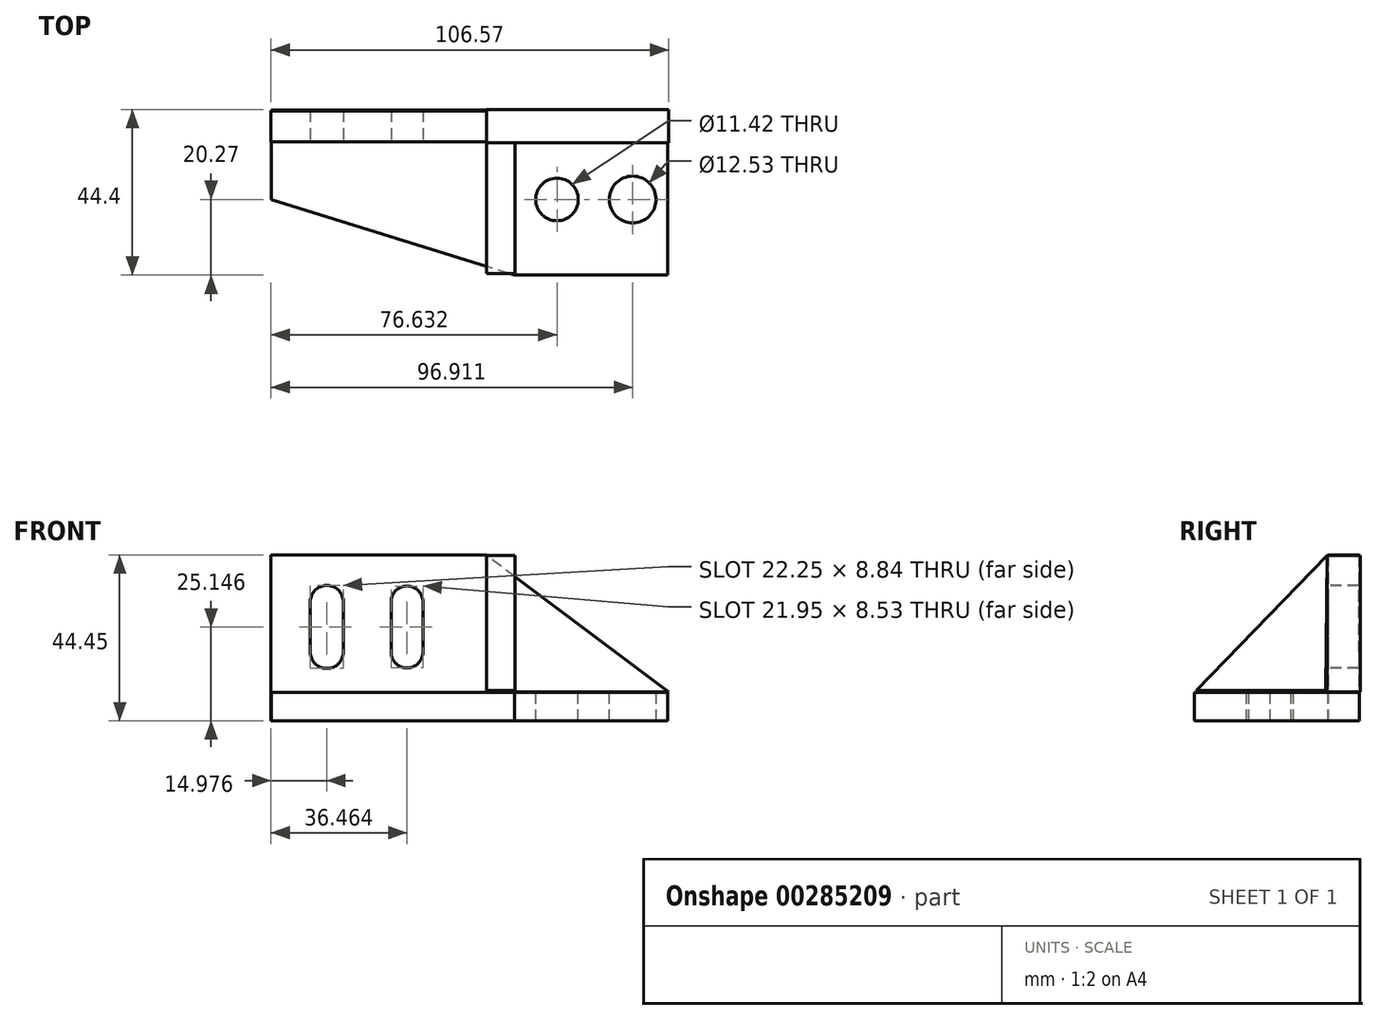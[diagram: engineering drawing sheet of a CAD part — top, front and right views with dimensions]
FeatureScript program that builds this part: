
annotation { "Feature Type Name" : "Feature", "Feature Type Description" : "" }
export const myFeature = defineFeature(function(context is Context, id is Id, definition is map)
    precondition{}
    {
        {
            var Q0;
            Q0=qCreatedBy(makeId("Top.planeOp"),FACE);
            var sketch = newSketch(context, id + "F0", { "sketchPlane" : qUnion([Q0])});
            skLineSegment(sketch, "E0", {"start": v(48.46, -20.27) * mm, "end": v(7.48, -20.27) * mm});
            skLineSegment(sketch, "E1", {"start": v(7.48, -20.27) * mm, "end": v(-57.74, 0) * mm});
            skLineSegment(sketch, "E2", {"start": v(-57.74, 0) * mm, "end": v(-57.74, 23.93) * mm});
            skLineSegment(sketch, "E3", {"start": v(-57.74, 23.93) * mm, "end": v(48.46, 23.93) * mm});
            skLineSegment(sketch, "E4", {"start": v(48.46, 23.93) * mm, "end": v(48.46, -20.27) * mm});
            skSolve(sketch);
        }
        {
            var Q0;
            Q0=makeQuery(id+"F0.imprint","IMPRINT",FACE,{"disambiguationData":[TD([[makeQuery(id+"F0.imprint","IMPRINT",EDGE,{"derivedFrom":sQuery(id+"F0.wireOp",EDGE,"E0")}),-1.0]])]});
            var sketch = newSketch(context, id + "F1", { "sketchPlane" : qUnion([Q0])});
            skLineSegment(sketch, "E5", {"start": v(-57.8, 15.5) * mm, "end": v(0, 15.5) * mm});
            skLineSegment(sketch, "E6", {"start": v(0, 15.5) * mm, "end": v(0, 23.75) * mm});
            skLineSegment(sketch, "E7", {"start": v(-57.8, 15.5) * mm, "end": v(-57.8, 23.75) * mm});
            skLineSegment(sketch, "E8", {"start": v(-57.8, 23.75) * mm, "end": v(0, 23.75) * mm});
            skSolve(sketch);
        }
        {
            var Q0;
            Q0 = qSketchRegion(id + "F1", true);
            extrude(context, id + "F2", {"entities" : qUnion([Q0]), "depth" : 44.45 * mm});
        }
        {
            var Q0;
            Q0=makeQuery(id+"F0.imprint","IMPRINT",FACE,{"disambiguationData":[TD([[makeQuery(id+"F0.imprint","IMPRINT",EDGE,{"derivedFrom":sQuery(id+"F0.wireOp",EDGE,"E0")}),-1.0]])]});
            extrude(context, id + "F3", {"entities" : qUnion([Q0]), "operationType" : NewBodyOperationType.ADD, "depth" : 7.62 * mm});
        }
        {
            var Q0;
            Q0=makeQuery(id+"F3.opExtrude","CAP_FACE",FACE,{"disambiguationData":[OSD([sQuery(id+"F0.wireOp",EDGE,"E0"),sQuery(id+"F0.wireOp",EDGE,"E1"),sQuery(id+"F0.wireOp",EDGE,"E2"),sQuery(id+"F0.wireOp",EDGE,"E3"),sQuery(id+"F0.wireOp",EDGE,"E4")])],"isStart":false});
            var sketch = newSketch(context, id + "F4", { "sketchPlane" : qUnion([Q0])});
            skSolve(sketch);
        }
        {
            var Q0;
            Q0=makeQuery(id+"F2.opExtrude","SWEPT_FACE",FACE,{"disambiguationData":[OSD([sQuery(id+"F1.wireOp",EDGE,"E5")])]});
            var sketch = newSketch(context, id + "F5", { "sketchPlane" : qUnion([Q0])});
            skSolve(sketch);
        }
        {
            var Q0;
            Q0=qCreatedBy(makeId("Front.planeOp"),FACE);
            var sketch = newSketch(context, id + "F6", { "sketchPlane" : qUnion([Q0])});
            skLineSegment(sketch, "E9", {"start": v(0, 44.35) * mm, "end": v(0, 7.77) * mm});
            skLineSegment(sketch, "E10", {"start": v(0, 7.77) * mm, "end": v(48.77, 7.77) * mm});
            skLineSegment(sketch, "E11", {"start": v(48.77, 7.77) * mm, "end": v(0, 44.35) * mm});
            skSolve(sketch);
        }
        {
            var Q0;
            Q0 = qSketchRegion(id + "F6", true);
            extrude(context, id + "F7", {"entities" : qUnion([Q0]), "oppositeDirection" : true, "depth" : 24.13 * mm});
        }
        {
            var Q0;
            Q0=makeQuery(id+"F7.opExtrude","CAP_FACE",FACE,{"disambiguationData":[OSD([sQuery(id+"F6.wireOp",EDGE,"E9"),sQuery(id+"F6.wireOp",EDGE,"E10"),sQuery(id+"F6.wireOp",EDGE,"E11")])],"isStart":true});
            extrude(context, id + "F8", {"entities" : qUnion([Q0]), "operationType" : NewBodyOperationType.REMOVE, "oppositeDirection" : true, "depth" : 15.24 * mm});
        }
        {
            var Q0;
            Q0=qCreatedBy(makeId("Right.planeOp"),FACE);
            var sketch = newSketch(context, id + "F9", { "sketchPlane" : qUnion([Q0])});
            skLineSegment(sketch, "E12", {"start": v(15.24, 44.35) * mm, "end": v(-19.81, 8.08) * mm});
            skLineSegment(sketch, "E13", {"start": v(-19.81, 8.08) * mm, "end": v(14.94, 8.08) * mm});
            skLineSegment(sketch, "E14", {"start": v(14.94, 8.08) * mm, "end": v(15.24, 44.35) * mm});
            skSolve(sketch);
        }
        {
            var Q0;
            Q0=makeQuery(id+"F9.imprint","IMPRINT",FACE,{"disambiguationData":[TD([[makeQuery(id+"F9.imprint","IMPRINT",EDGE,{"derivedFrom":sQuery(id+"F9.wireOp",EDGE,"E12")}),1.0]])]});
            extrude(context, id + "F10", {"entities" : qUnion([Q0]), "operationType" : NewBodyOperationType.ADD, "depth" : 7.62 * mm});
        }
        {
            var Q0;
            {var subQ0=sQuery(id+"F1.wireOp",EDGE,"E5");Q0=makeQuery(id+"F5.imprint","IMPRINT",FACE,{"disambiguationData":[TD([[makeQuery(id+"F5.imprint","IMPRINT",EDGE,{"derivedFrom":makeQuery(id+"F2.opExtrude","CAP_EDGE",EDGE,{"disambiguationData":[OSD([subQ0])],"isStart":false})}),-1.0]])]});}
            var sketch = newSketch(context, id + "F11", { "sketchPlane" : qUnion([Q0])});
            skLineSegment(sketch, "E15", {"start": v(-47.24, 31.85) * mm, "end": v(-47.24, 18.44) * mm});
            skLineSegment(sketch, "E16", {"start": v(-47.24, 18.44) * mm, "end": v(-47.24, 31.85) * mm});
            skLineSegment(sketch, "E17", {"start": v(-38.4, 31.85) * mm, "end": v(-38.4, 18.44) * mm});
            skLineSegment(sketch, "E18", {"start": v(-38.4, 18.44) * mm, "end": v(-38.4, 31.85) * mm});
            skLineSegment(sketch, "E19", {"start": v(-25.6, 31.85) * mm, "end": v(-25.6, 18.44) * mm});
            skLineSegment(sketch, "E20", {"start": v(-25.6, 18.44) * mm, "end": v(-25.6, 31.85) * mm});
            skLineSegment(sketch, "E21", {"start": v(-17.07, 31.85) * mm, "end": v(-17.07, 18.44) * mm});
            skLineSegment(sketch, "E22", {"start": v(-17.07, 18.44) * mm, "end": v(-17.07, 31.85) * mm});
            skArc(sketch, "E23", {"start": v(-47.24, 18.44) * mm, "mid": v(-42.82, 14.02) * mm, "end": v(-38.4, 18.44) * mm});
            skArc(sketch, "E24", {"start": v(-25.6, 18.44) * mm, "mid": v(-21.34, 14.17) * mm, "end": v(-17.07, 18.44) * mm});
            skArc(sketch, "E25", {"start": v(-38.4, 31.85) * mm, "mid": v(-42.82, 36.27) * mm, "end": v(-47.24, 31.85) * mm});
            skArc(sketch, "E26", {"start": v(-17.07, 31.85) * mm, "mid": v(-21.34, 36.12) * mm, "end": v(-25.6, 31.85) * mm});
            skSolve(sketch);
        }
        {
            var Q0;
            Q0 = qSketchRegion(id + "F11", true);
            extrude(context, id + "F12", {"entities" : qUnion([Q0]), "operationType" : NewBodyOperationType.REMOVE, "oppositeDirection" : true, "depth" : 127 * mm});
        }
        {
            var Q0;
            {var subQ3=sQuery(id+"F0.wireOp",EDGE,"E0");Q0=makeQuery(id+"F4.imprint","IMPRINT",FACE,{"disambiguationData":[TD([[makeQuery(id+"F4.imprint","IMPRINT",EDGE,{"derivedFrom":makeQuery(id+"F3.opExtrude","CAP_EDGE",EDGE,{"disambiguationData":[OSD([subQ3])],"isStart":false})}),-1.0]])]});}
            var sketch = newSketch(context, id + "F13", { "sketchPlane" : qUnion([Q0])});
            skCircle(sketch, "E27", {"center": v(18.83, 0) * mm, "radius": 5.7 * mm});
            skSolve(sketch);
        }
        {
            var Q0;
            Q0 = qSketchRegion(id + "F13", true);
            extrude(context, id + "F14", {"entities" : qUnion([Q0]), "operationType" : NewBodyOperationType.REMOVE, "oppositeDirection" : true, "depth" : 127 * mm});
        }
        {
            var Q0;
            {var subQ3=sQuery(id+"F0.wireOp",EDGE,"E0");Q0=makeQuery(id+"F4.imprint","IMPRINT",FACE,{"disambiguationData":[TD([[makeQuery(id+"F4.imprint","IMPRINT",EDGE,{"derivedFrom":makeQuery(id+"F3.opExtrude","CAP_EDGE",EDGE,{"disambiguationData":[OSD([subQ3])],"isStart":false})}),-1.0]])]});}
            var sketch = newSketch(context, id + "F15", { "sketchPlane" : qUnion([Q0])});
            skCircle(sketch, "E28", {"center": v(39.11, 0) * mm, "radius": 6.26 * mm});
            skSolve(sketch);
        }
        {
            var Q0;
            Q0 = qSketchRegion(id + "F15", true);
            extrude(context, id + "F16", {"entities" : qUnion([Q0]), "operationType" : NewBodyOperationType.REMOVE, "oppositeDirection" : true, "depth" : 127 * mm});
        }
    });
